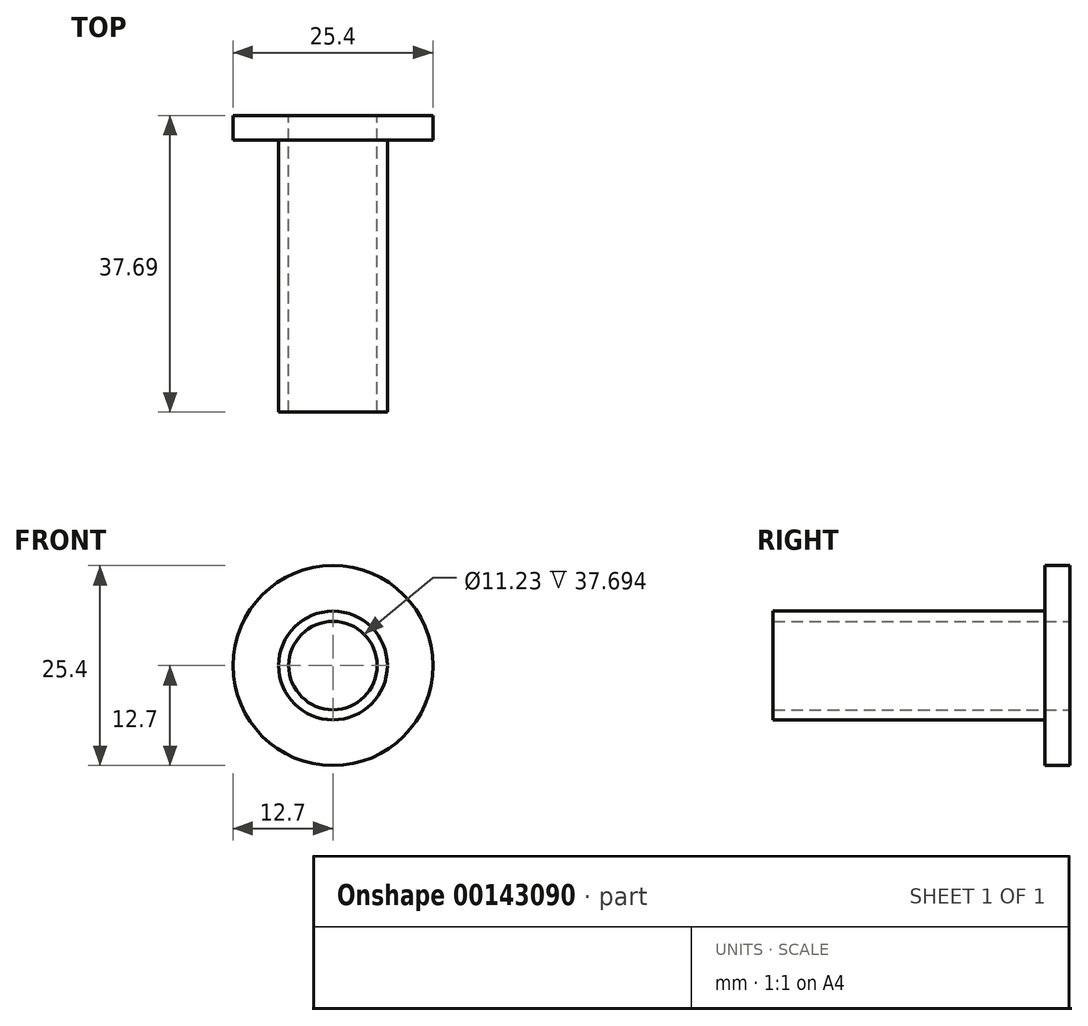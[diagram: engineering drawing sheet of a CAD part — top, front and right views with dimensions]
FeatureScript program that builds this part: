
annotation { "Feature Type Name" : "Feature", "Feature Type Description" : "" }
export const myFeature = defineFeature(function(context is Context, id is Id, definition is map)
    precondition{}
    {
        {
            var Q0;
            Q0=qCreatedBy(makeId("Front.planeOp"),FACE);
            var sketch = newSketch(context, id + "F0", { "sketchPlane" : qUnion([Q0])});
            skCircle(sketch, "E0", {"center": v(0, 0) * mm, "radius": 12.7 * mm});
            skSolve(sketch);
        }
        {
            var Q0;
            Q0=makeQuery(id+"F0.imprint","IMPRINT",FACE,{"disambiguationData":[TD([[makeQuery(id+"F0.imprint","IMPRINT",EDGE,{"derivedFrom":sQuery(id+"F0.wireOp",EDGE,"E0")}),1.0]])]});
            extrude(context, id + "F1", {"entities" : qUnion([Q0]), "depth" : 3.15 * mm});
        }
        {
            var Q0;
            Q0=makeQuery(id+"F1.opExtrude","CAP_FACE",FACE,{"disambiguationData":[OSD([sQuery(id+"F0.wireOp",EDGE,"E0")])],"isStart":false});
            var sketch = newSketch(context, id + "F2", { "sketchPlane" : qUnion([Q0])});
            skCircle(sketch, "E1", {"center": v(0, 0) * mm, "radius": 6.9 * mm});
            skSolve(sketch);
        }
        {
            var Q0;
            Q0 = qSketchRegion(id + "F2", true);
            extrude(context, id + "F3", {"entities" : qUnion([Q0]), "operationType" : NewBodyOperationType.ADD, "depth" : 34.54 * mm});
        }
        {
            var Q0;
            Q0=makeQuery(id+"F1.opExtrude","CAP_FACE",FACE,{"disambiguationData":[OSD([sQuery(id+"F0.wireOp",EDGE,"E0")])],"isStart":true});
            var sketch = newSketch(context, id + "F4", { "sketchPlane" : qUnion([Q0])});
            skCircle(sketch, "E2", {"center": v(0, 0) * mm, "radius": 5.61 * mm});
            skSolve(sketch);
        }
        {
            var Q0;
            Q0 = qSketchRegion(id + "F4", true);
            extrude(context, id + "F5", {"entities" : qUnion([Q0]), "operationType" : NewBodyOperationType.REMOVE, "endBound" : BoundingType.THROUGH_ALL, "oppositeDirection" : true, "depth" : 25.4 * mm});
        }
    });
